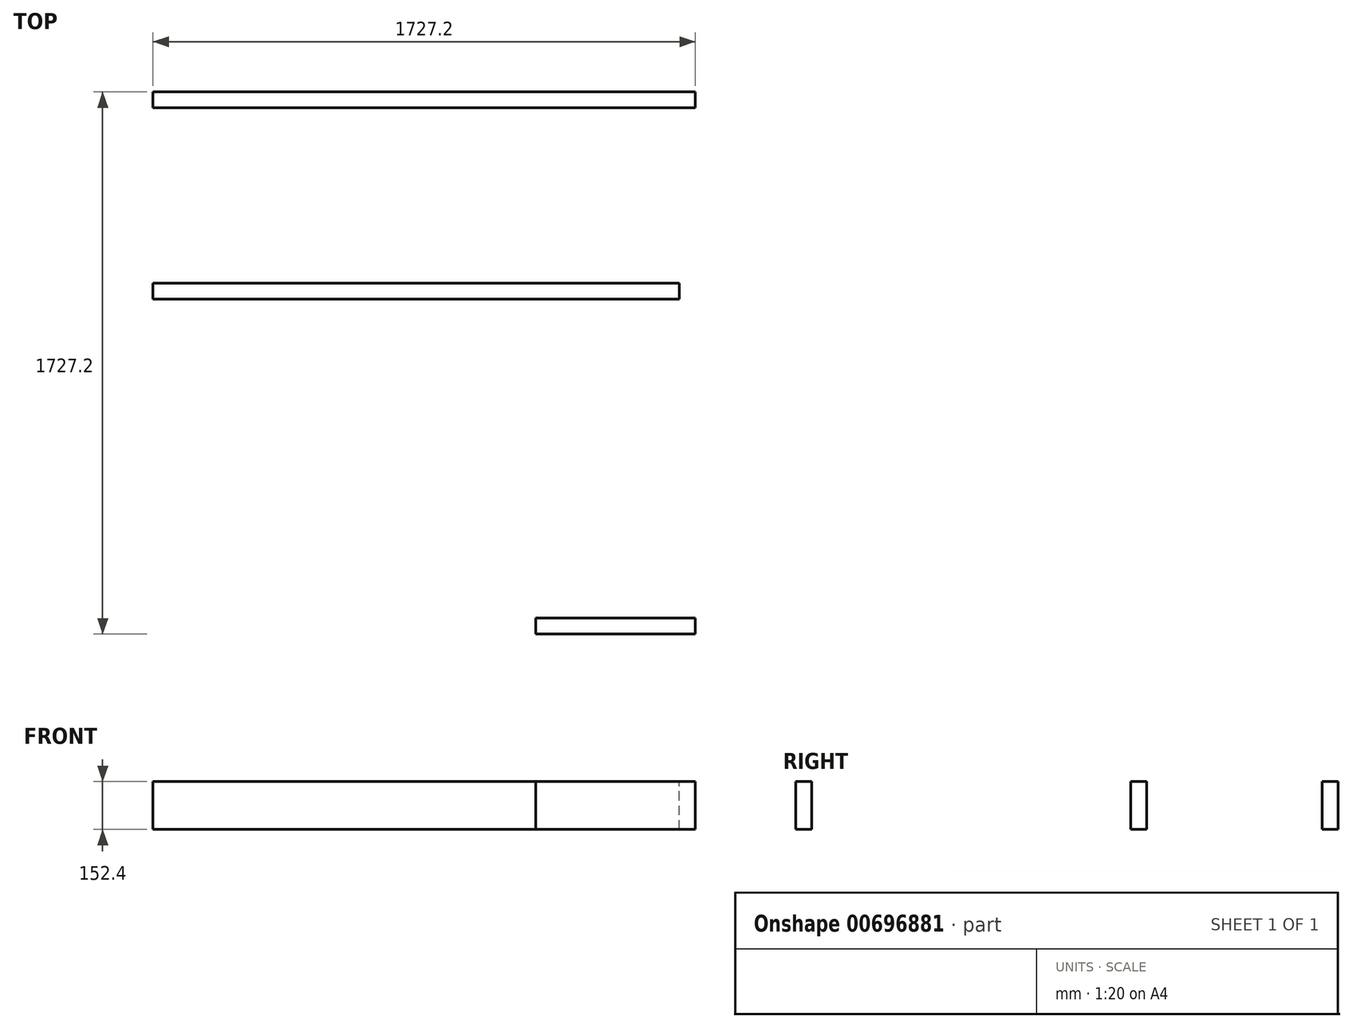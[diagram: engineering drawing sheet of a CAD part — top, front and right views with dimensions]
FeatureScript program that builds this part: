
annotation { "Feature Type Name" : "Feature", "Feature Type Description" : "" }
export const myFeature = defineFeature(function(context is Context, id is Id, definition is map)
    precondition{}
    {
        {
            var Q0;
            Q0=qCreatedBy(makeId("Top.planeOp"),FACE);
            var sketch = newSketch(context, id + "F0", { "sketchPlane" : qUnion([Q0])});
            skLineSegment(sketch, "E0.bottom", {"start": v(0, 0) * mm, "end": v(1727.2, 0) * mm});
            skLineSegment(sketch, "E0.top", {"start": v(0, -50.8) * mm, "end": v(1727.2, -50.8) * mm});
            skLineSegment(sketch, "E0.left", {"start": v(0, 0) * mm, "end": v(0, -50.8) * mm});
            skLineSegment(sketch, "E0.right", {"start": v(1727.2, 0) * mm, "end": v(1727.2, -50.8) * mm});
            skLineSegment(sketch, "E1.bottom", {"start": v(0, -50.8) * mm, "end": v(50.8, -50.8) * mm});
            skLineSegment(sketch, "E1.top", {"start": v(0, -609.6) * mm, "end": v(50.8, -609.6) * mm});
            skLineSegment(sketch, "E1.left", {"start": v(0, -50.8) * mm, "end": v(0, -609.6) * mm});
            skLineSegment(sketch, "E1.right", {"start": v(50.8, -50.8) * mm, "end": v(50.8, -609.6) * mm});
            skLineSegment(sketch, "E2.bottom", {"start": v(1727.2, -50.8) * mm, "end": v(1676.4, -50.8) * mm});
            skLineSegment(sketch, "E2.top", {"start": v(1727.2, -1676.4) * mm, "end": v(1676.4, -1676.4) * mm});
            skLineSegment(sketch, "E2.left", {"start": v(1727.2, -50.8) * mm, "end": v(1727.2, -1676.4) * mm});
            skLineSegment(sketch, "E2.right", {"start": v(1676.4, -50.8) * mm, "end": v(1676.4, -1676.4) * mm});
            skLineSegment(sketch, "E3.bottom", {"start": v(1727.2, -1676.4) * mm, "end": v(1219.2, -1676.4) * mm});
            skLineSegment(sketch, "E3.top", {"start": v(1727.2, -1727.2) * mm, "end": v(1219.2, -1727.2) * mm});
            skLineSegment(sketch, "E3.left", {"start": v(1727.2, -1676.4) * mm, "end": v(1727.2, -1727.2) * mm});
            skLineSegment(sketch, "E3.right", {"start": v(1219.2, -1676.4) * mm, "end": v(1219.2, -1727.2) * mm});
            skLineSegment(sketch, "E4.bottom", {"start": v(0, -609.6) * mm, "end": v(1676.4, -609.6) * mm});
            skLineSegment(sketch, "E4.top", {"start": v(0, -660.4) * mm, "end": v(1676.4, -660.4) * mm});
            skLineSegment(sketch, "E4.left", {"start": v(0, -609.6) * mm, "end": v(0, -660.4) * mm});
            skLineSegment(sketch, "E4.right", {"start": v(1676.4, -609.6) * mm, "end": v(1676.4, -660.4) * mm});
            skLineSegment(sketch, "E5.bottom", {"start": v(1219.2, -1676.4) * mm, "end": v(1270, -1676.4) * mm});
            skLineSegment(sketch, "E5.top", {"start": v(1219.2, -660.4) * mm, "end": v(1270, -660.4) * mm});
            skLineSegment(sketch, "E5.left", {"start": v(1219.2, -1676.4) * mm, "end": v(1219.2, -660.4) * mm});
            skLineSegment(sketch, "E5.right", {"start": v(1270, -1676.4) * mm, "end": v(1270, -660.4) * mm});
            skSolve(sketch);
        }
        {
            var Q0;
            Q0=makeQuery(id+"F0.imprint","IMPRINT",FACE,{"disambiguationData":[TD([[makeQuery(id+"F0.imprint","IMPRINT",EDGE,{"derivedFrom":sQuery(id+"F0.wireOp",EDGE,"E0.bottom")}),-1.0]])]});
            var Q1;
            {var subQ4=sQuery(id+"F0.wireOp",EDGE,"E2.bottom");Q1=makeQuery(id+"F0.imprint","IMPRINT",FACE,{"disambiguationData":[TD([[makeQuery(id+"F0.imprint","IMPRINT",EDGE,{"derivedFrom":subQ4}),1.0]])]});}
            var Q2;
            Q2=makeQuery(id+"F0.imprint","IMPRINT",FACE,{"disambiguationData":[TD([[makeQuery(id+"F0.imprint","IMPRINT",EDGE,{"derivedFrom":sQuery(id+"F0.wireOp",EDGE,"E1.bottom")}),-1.0]])]});
            var Q3;
            {var subQ4=sQuery(id+"F0.wireOp",EDGE,"E4.left");Q3=makeQuery(id+"F0.imprint","IMPRINT",FACE,{"disambiguationData":[TD([[makeQuery(id+"F0.imprint","IMPRINT",EDGE,{"derivedFrom":subQ4}),1.0]])]});}
            var Q4;
            Q4=makeQuery(id+"F0.imprint","IMPRINT",FACE,{"disambiguationData":[TD([[makeQuery(id+"F0.imprint","IMPRINT",EDGE,{"derivedFrom":sQuery(id+"F0.wireOp",EDGE,"E3.top")}),-1.0]])]});
            var Q5;
            Q5=makeQuery(id+"F0.imprint","IMPRINT",FACE,{"disambiguationData":[TD([[makeQuery(id+"F0.imprint","IMPRINT",EDGE,{"derivedFrom":sQuery(id+"F0.wireOp",EDGE,"E5.bottom")}),1.0]])]});
            extrude(context, id + "F1", {"entities" : qUnion([Q0, Q1, Q2, Q3, Q4, Q5]), "oppositeDirection" : true, "depth" : 152.4 * mm, "offsetDistance" : 25.4 * mm});
        }
    });
